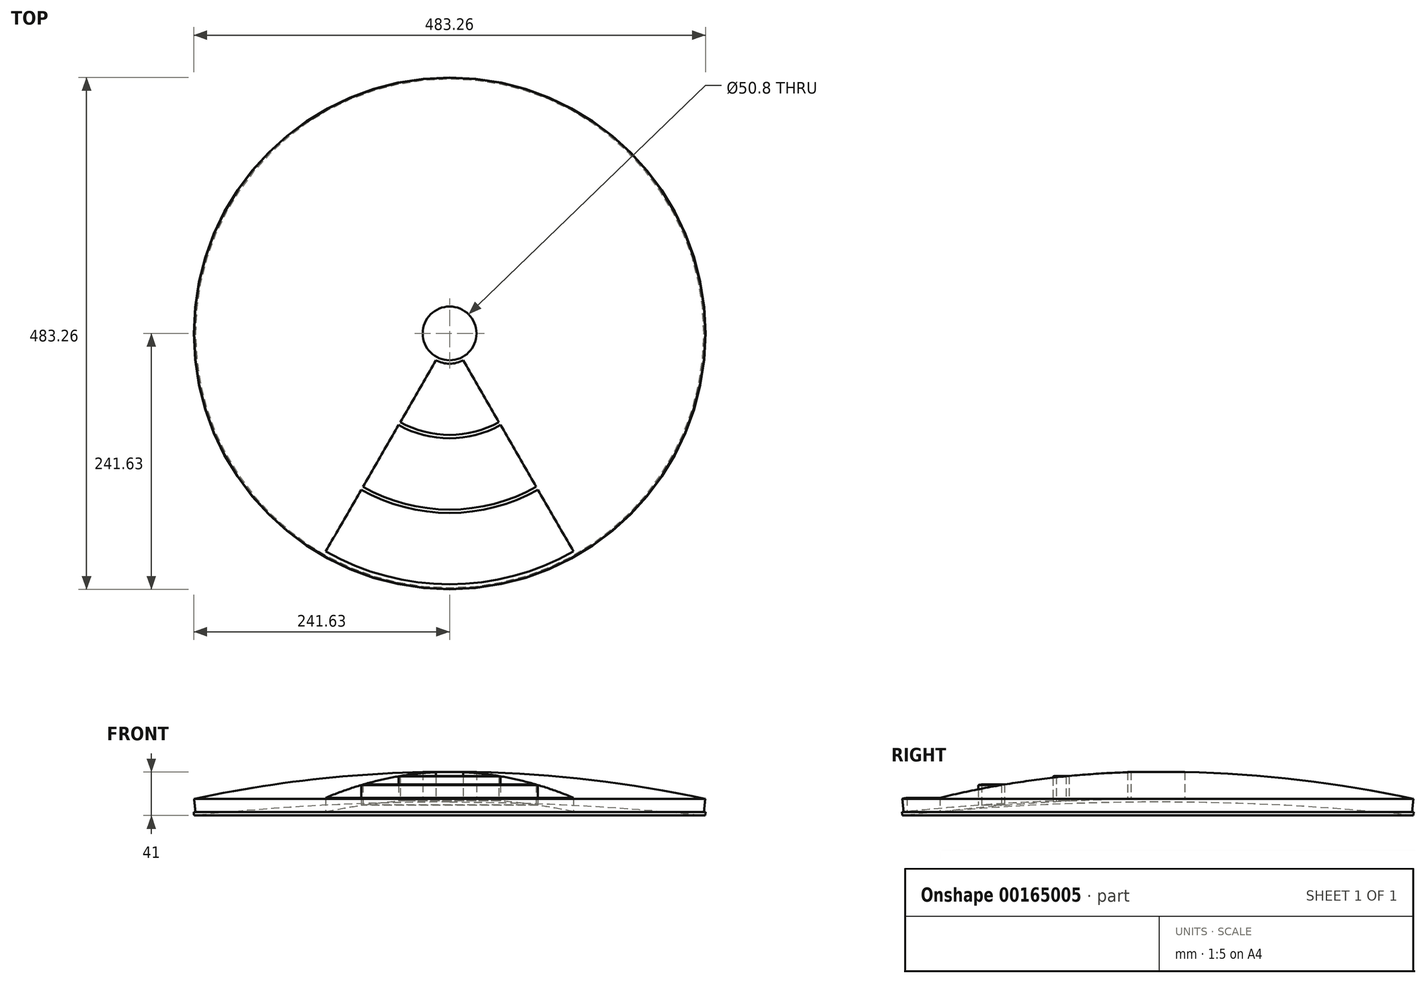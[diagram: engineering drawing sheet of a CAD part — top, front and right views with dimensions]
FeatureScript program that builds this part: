
annotation { "Feature Type Name" : "Feature", "Feature Type Description" : "" }
export const myFeature = defineFeature(function(context is Context, id is Id, definition is map)
    precondition{}
    {
        {
            var Q0;
            Q0=qCreatedBy(makeId("Front.planeOp"),FACE);
            var sketch = newSketch(context, id + "F0", { "sketchPlane" : qUnion([Q0])});
            skLineSegment(sketch, "E0", {"start": v(0, 0) * mm, "end": v(0, 15.88) * mm, "construction": true});
            skArc(sketch, "E1", {"start": v(239.96, 3.16) * mm, "mid": v(120.15, 12.7) * mm, "end": v(0, 15.87) * mm});
            skArc(sketch, "E2", {"start": v(0, 15.87) * mm, "mid": v(-120.15, 12.7) * mm, "end": v(-239.96, 3.16) * mm, "construction": true});
            skLineSegment(sketch, "E3", {"start": v(239.96, 3.16) * mm, "end": v(241.3, 15.79) * mm});
            skArc(sketch, "E4", {"start": v(241.3, 15.79) * mm, "mid": v(121.32, 34.89) * mm, "end": v(0, 41.27) * mm});
            skLineSegment(sketch, "E5", {"start": v(239.96, 3.16) * mm, "end": v(252.59, 1.81) * mm, "construction": true});
            skLineSegment(sketch, "E6", {"start": v(0, 15.88) * mm, "end": v(0, 41.28) * mm});
            skLineSegment(sketch, "E7", {"start": v(-239.96, 3.16) * mm, "end": v(-252.59, 1.81) * mm, "construction": true});
            skLineSegment(sketch, "E8", {"start": v(-239.96, 3.16) * mm, "end": v(-241.3, 15.79) * mm, "construction": true});
            skArc(sketch, "E9", {"start": v(0, 41.27) * mm, "mid": v(-121.32, 34.89) * mm, "end": v(-241.3, 15.79) * mm, "construction": true});
            skLineSegment(sketch, "E10", {"start": v(239.96, 3.16) * mm, "end": v(239.62, 0) * mm, "construction": true});
            skLineSegment(sketch, "E11", {"start": v(239.62, 0) * mm, "end": v(0, 0) * mm, "construction": true});
            skLineSegment(sketch, "E12", {"start": v(0, 0) * mm, "end": v(-239.62, 0) * mm, "construction": true});
            skLineSegment(sketch, "E13", {"start": v(-239.62, 0) * mm, "end": v(-239.96, 3.16) * mm, "construction": true});
            skSolve(sketch);
        }
        {
            var Q0;
            Q0=qCreatedBy(makeId("Top.planeOp"),FACE);
            var sketch = newSketch(context, id + "F1", { "sketchPlane" : qUnion([Q0])});
            skCircle(sketch, "E14", {"center": v(0, 0) * mm, "radius": 25.4 * mm});
            skSolve(sketch);
        }
        {
            var Q0;
            Q0=makeQuery(id+"F0.imprint","IMPRINT",FACE,{"disambiguationData":[TD([[makeQuery(id+"F0.imprint","IMPRINT",EDGE,{"derivedFrom":sQuery(id+"F0.wireOp",EDGE,"E1")}),-1.0]])]});
            var Q1;
            Q1=sQuery(id+"F1.wireOp",EDGE,"E14");
            revolve(context, id + "F2", {"entities" : qUnion([Q0]), "axis" : qUnion([Q1]), "revolveType" : RevolveType.FULL});
        }
        {
            var Q0;
            Q0 = qSketchRegion(id + "F1", true);
            var Q1;
            Q1=makeQuery(id+"F2.opRevolve","SWEPT_FACE",FACE,{"disambiguationData":[OSD([sQuery(id+"F0.wireOp",EDGE,"E4")])]});
            extrude(context, id + "F3", {"entities" : qUnion([Q0]), "operationType" : NewBodyOperationType.REMOVE, "endBound" : BoundingType.UP_TO_SURFACE, "endBoundEntityFace" : qUnion([Q1]), "depth" : 25.4 * mm});
        }
        {
            var Q0;
            Q0=qCreatedBy(makeId("Top.planeOp"),FACE);
            var sketch = newSketch(context, id + "F4", { "sketchPlane" : qUnion([Q0])});
            skLineSegment(sketch, "E15", {"start": v(0, -3.17) * mm, "end": v(0, -239.96) * mm, "construction": true});
            skArc(sketch, "E16", {"start": v(-118.6, -208.6) * mm, "mid": v(0, -239.96) * mm, "end": v(118.6, -208.6) * mm, "construction": true});
            skLineSegment(sketch, "E17", {"start": v(-118.6, -208.6) * mm, "end": v(-117.01, -205.85) * mm, "construction": true});
            skLineSegment(sketch, "E18", {"start": v(118.6, -208.6) * mm, "end": v(117.01, -205.85) * mm, "construction": true});
            skArc(sketch, "E19", {"start": v(-117.01, -205.85) * mm, "mid": v(0, -236.78) * mm, "end": v(117.01, -205.85) * mm});
            skLineSegment(sketch, "E20", {"start": v(-117.01, -205.85) * mm, "end": v(-83.36, -147.57) * mm});
            skLineSegment(sketch, "E21", {"start": v(117.01, -205.85) * mm, "end": v(83.36, -147.57) * mm});
            skArc(sketch, "E22", {"start": v(-83.36, -147.57) * mm, "mid": v(0, -169.49) * mm, "end": v(83.36, -147.57) * mm});
            skArc(sketch, "E23", {"start": v(-81.78, -144.82) * mm, "mid": v(0, -166.31) * mm, "end": v(81.78, -144.82) * mm});
            skLineSegment(sketch, "E24", {"start": v(-83.36, -147.57) * mm, "end": v(-81.78, -144.82) * mm, "construction": true});
            skLineSegment(sketch, "E25", {"start": v(81.78, -144.82) * mm, "end": v(83.36, -147.57) * mm, "construction": true});
            skLineSegment(sketch, "E26", {"start": v(-81.78, -144.82) * mm, "end": v(-48.13, -86.53) * mm});
            skLineSegment(sketch, "E27", {"start": v(81.78, -144.82) * mm, "end": v(48.13, -86.53) * mm});
            skArc(sketch, "E28", {"start": v(-48.13, -86.53) * mm, "mid": v(0, -99.02) * mm, "end": v(48.13, -86.53) * mm});
            skLineSegment(sketch, "E29", {"start": v(-48.13, -86.53) * mm, "end": v(-46.54, -83.78) * mm, "construction": true});
            skLineSegment(sketch, "E30", {"start": v(48.13, -86.53) * mm, "end": v(46.54, -83.78) * mm, "construction": true});
            skArc(sketch, "E31", {"start": v(-46.54, -83.78) * mm, "mid": v(0, -95.84) * mm, "end": v(46.54, -83.78) * mm});
            skLineSegment(sketch, "E32", {"start": v(-46.54, -83.78) * mm, "end": v(-12.9, -25.5) * mm});
            skLineSegment(sketch, "E33", {"start": v(46.54, -83.78) * mm, "end": v(12.9, -25.5) * mm});
            skLineSegment(sketch, "E34", {"start": v(0, -3.17) * mm, "end": v(12.9, -25.5) * mm, "construction": true});
            skArc(sketch, "E35", {"start": v(-12.9, -25.5) * mm, "mid": v(0, -28.57) * mm, "end": v(12.9, -25.5) * mm});
            skLineSegment(sketch, "E36", {"start": v(-64.95, -115.68) * mm, "end": v(-66.33, -114.88) * mm, "construction": true});
            skLineSegment(sketch, "E37", {"start": v(-66.33, -114.88) * mm, "end": v(0, 0) * mm, "construction": true});
            skLineSegment(sketch, "E38", {"start": v(0, 0) * mm, "end": v(0, -3.18) * mm, "construction": true});
            skLineSegment(sketch, "E39", {"start": v(-12.9, -25.5) * mm, "end": v(0, -3.17) * mm, "construction": true});
            skLineSegment(sketch, "E40", {"start": v(64.95, -115.68) * mm, "end": v(66.33, -114.88) * mm, "construction": true});
            skLineSegment(sketch, "E41", {"start": v(66.33, -114.88) * mm, "end": v(0, 0) * mm, "construction": true});
            skSolve(sketch);
        }
        {
            var Q0;
            Q0 = qSketchRegion(id + "F4", true);
            var Q1;
            Q1=makeQuery(id+"F2.opRevolve","SWEPT_FACE",FACE,{"disambiguationData":[OSD([sQuery(id+"F0.wireOp",EDGE,"E4")])]});
            extrude(context, id + "F5", {"entities" : qUnion([Q0]), "operationType" : NewBodyOperationType.REMOVE, "endBound" : BoundingType.UP_TO_SURFACE, "endBoundEntityFace" : qUnion([Q1]), "depth" : 25.4 * mm});
        }
        {
            var Q0;
            Q0=qCreatedBy(makeId("Front.planeOp"),FACE);
            var sketch = newSketch(context, id + "F6", { "sketchPlane" : qUnion([Q0])});
            skLineSegment(sketch, "E42", {"start": v(0, 0) * mm, "end": v(0, 12.7) * mm});
            skLineSegment(sketch, "E43", {"start": v(0, 0) * mm, "end": v(241.3, 0) * mm});
            skArc(sketch, "E44", {"start": v(241.3, 0) * mm, "mid": v(120.82, 9.52) * mm, "end": v(0, 12.7) * mm});
            skLineSegment(sketch, "E45", {"start": v(0, 0) * mm, "end": v(-241.3, 0) * mm, "construction": true});
            skArc(sketch, "E46", {"start": v(0, 12.7) * mm, "mid": v(-120.82, 9.52) * mm, "end": v(-241.3, 0) * mm, "construction": true});
            skLineSegment(sketch, "E47", {"start": v(0, 12.7) * mm, "end": v(0, 15.88) * mm});
            skLineSegment(sketch, "E48", {"start": v(241.3, 0) * mm, "end": v(241.63, 3.16) * mm});
            skLineSegment(sketch, "E49", {"start": v(241.3, 0) * mm, "end": v(244.46, -0.33) * mm, "construction": true});
            skArc(sketch, "E50", {"start": v(241.63, 3.16) * mm, "mid": v(120.98, 12.7) * mm, "end": v(0, 15.87) * mm});
            skSolve(sketch);
        }
        {
            var Q0;
            Q0=makeQuery(id+"F6.imprint","IMPRINT",FACE,{"disambiguationData":[TD([[makeQuery(id+"F6.imprint","IMPRINT",EDGE,{"derivedFrom":sQuery(id+"F6.wireOp",EDGE,"E44")}),-1.0]])]});
            var Q1;
            Q1=makeQuery(id+"F2.opRevolve","SWEPT_FACE",FACE,{"disambiguationData":[OSD([sQuery(id+"F0.wireOp",EDGE,"E3")])]});
            revolve(context, id + "F7", {"operationType" : NewBodyOperationType.ADD, "entities" : qUnion([Q0]), "axis" : qUnion([Q1]), "revolveType" : RevolveType.FULL});
        }
    });
